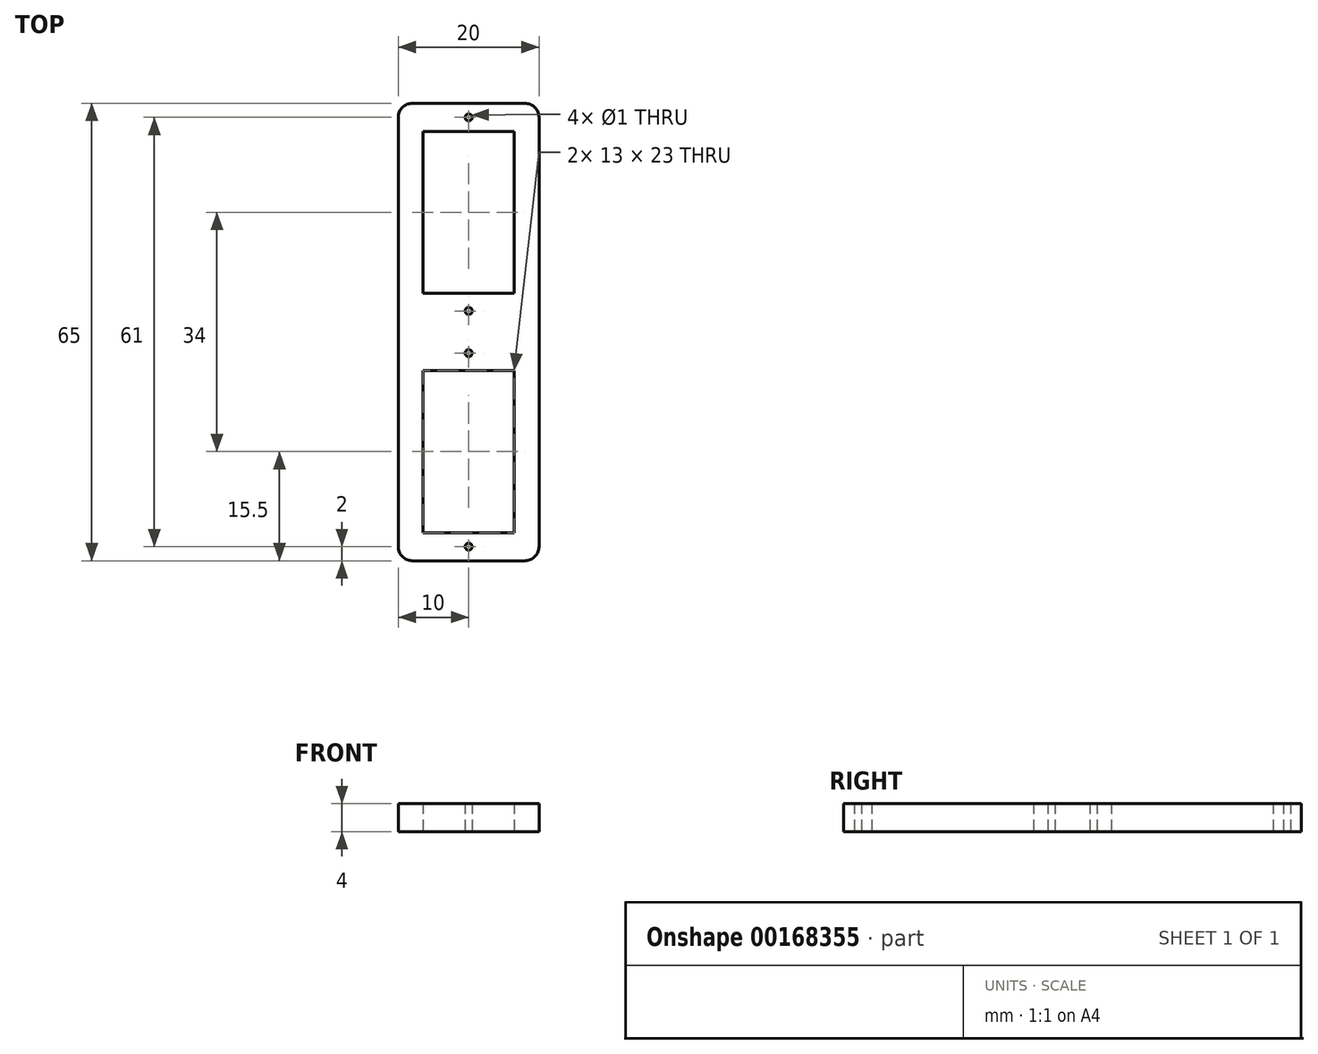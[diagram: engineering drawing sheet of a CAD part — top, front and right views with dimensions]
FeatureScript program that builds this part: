
annotation { "Feature Type Name" : "Feature", "Feature Type Description" : "" }
export const myFeature = defineFeature(function(context is Context, id is Id, definition is map)
    precondition{}
    {
        {
            var Q0;
            Q0=qCreatedBy(makeId("Top.planeOp"),FACE);
            var sketch = newSketch(context, id + "F0", { "sketchPlane" : qUnion([Q0])});
            skLineSegment(sketch, "E0.bottom", {"start": v(-10, 32.5) * mm, "end": v(10, 32.5) * mm});
            skLineSegment(sketch, "E0.top", {"start": v(-10, -32.5) * mm, "end": v(10, -32.5) * mm});
            skLineSegment(sketch, "E0.left", {"start": v(-10, 32.5) * mm, "end": v(-10, -32.5) * mm});
            skLineSegment(sketch, "E0.right", {"start": v(10, 32.5) * mm, "end": v(10, -32.5) * mm});
            skPoint(sketch, "E0.middle", {"position": v(0, 0) * mm});
            skLineSegment(sketch, "E1.bottom", {"start": v(6.5, 28.5) * mm, "end": v(-6.5, 28.5) * mm});
            skLineSegment(sketch, "E1.top", {"start": v(6.5, 5.5) * mm, "end": v(-6.5, 5.5) * mm});
            skLineSegment(sketch, "E1.left", {"start": v(6.5, 28.5) * mm, "end": v(6.5, 5.5) * mm});
            skLineSegment(sketch, "E1.right", {"start": v(-6.5, 28.5) * mm, "end": v(-6.5, 5.5) * mm});
            skPoint(sketch, "E1.middle", {"position": v(0, 17) * mm});
            skLineSegment(sketch, "E2.MirrorCS", {"start": v(-6.5, -28.5) * mm, "end": v(-6.5, -5.5) * mm});
            skLineSegment(sketch, "E3.MirrorCS", {"start": v(6.5, -28.5) * mm, "end": v(-6.5, -28.5) * mm});
            skLineSegment(sketch, "E4.MirrorCS", {"start": v(6.5, -28.5) * mm, "end": v(6.5, -5.5) * mm});
            skLineSegment(sketch, "E5.MirrorCS", {"start": v(6.5, -5.5) * mm, "end": v(-6.5, -5.5) * mm});
            skPoint(sketch, "E6", {"position": v(0, -30.5) * mm});
            skPoint(sketch, "E7.MirrorP", {"position": v(0, 30.5) * mm});
            skPoint(sketch, "E8", {"position": v(0, 3) * mm});
            skCircle(sketch, "E9", {"center": v(0, 30.5) * mm, "radius": 0.5 * mm});
            skCircle(sketch, "E10", {"center": v(0, 3) * mm, "radius": 0.5 * mm});
            skPoint(sketch, "E11.MirrorP", {"position": v(0, -3) * mm});
            skCircle(sketch, "E12", {"center": v(0, -30.5) * mm, "radius": 0.5 * mm});
            skCircle(sketch, "E13", {"center": v(0, -3) * mm, "radius": 0.5 * mm});
            skSolve(sketch);
        }
        {
            var Q0;
            Q0 = qSketchRegion(id + "F0", true);
            extrude(context, id + "F1", {"entities" : qUnion([Q0]), "depth" : 4 * mm});
        }
        {
            var Q0;
            Q0=makeQuery(id+"F1.opExtrude","SWEPT_EDGE",EDGE,{"disambiguationData":[OSD([sQuery(id+"F0.wireOp",EDGE,"E0.bottom"),sQuery(id+"F0.wireOp",EDGE,"E0.right")])]});
            var Q1;
            Q1=makeQuery(id+"F1.opExtrude","SWEPT_EDGE",EDGE,{"disambiguationData":[OSD([sQuery(id+"F0.wireOp",EDGE,"E0.top"),sQuery(id+"F0.wireOp",EDGE,"E0.right")])]});
            var Q2;
            Q2=makeQuery(id+"F1.opExtrude","SWEPT_EDGE",EDGE,{"disambiguationData":[OSD([sQuery(id+"F0.wireOp",EDGE,"E0.top"),sQuery(id+"F0.wireOp",EDGE,"E0.left")])]});
            var Q3;
            Q3=makeQuery(id+"F1.opExtrude","SWEPT_EDGE",EDGE,{"disambiguationData":[OSD([sQuery(id+"F0.wireOp",EDGE,"E0.bottom"),sQuery(id+"F0.wireOp",EDGE,"E0.left")])]});
            fillet(context, id + "F2", {"entities" : qUnion([Q0, Q1, Q2, Q3]), "radius" : 2 * mm, "tangentPropagation" : true, "allowEdgeOverflow" : false});
        }
    });
